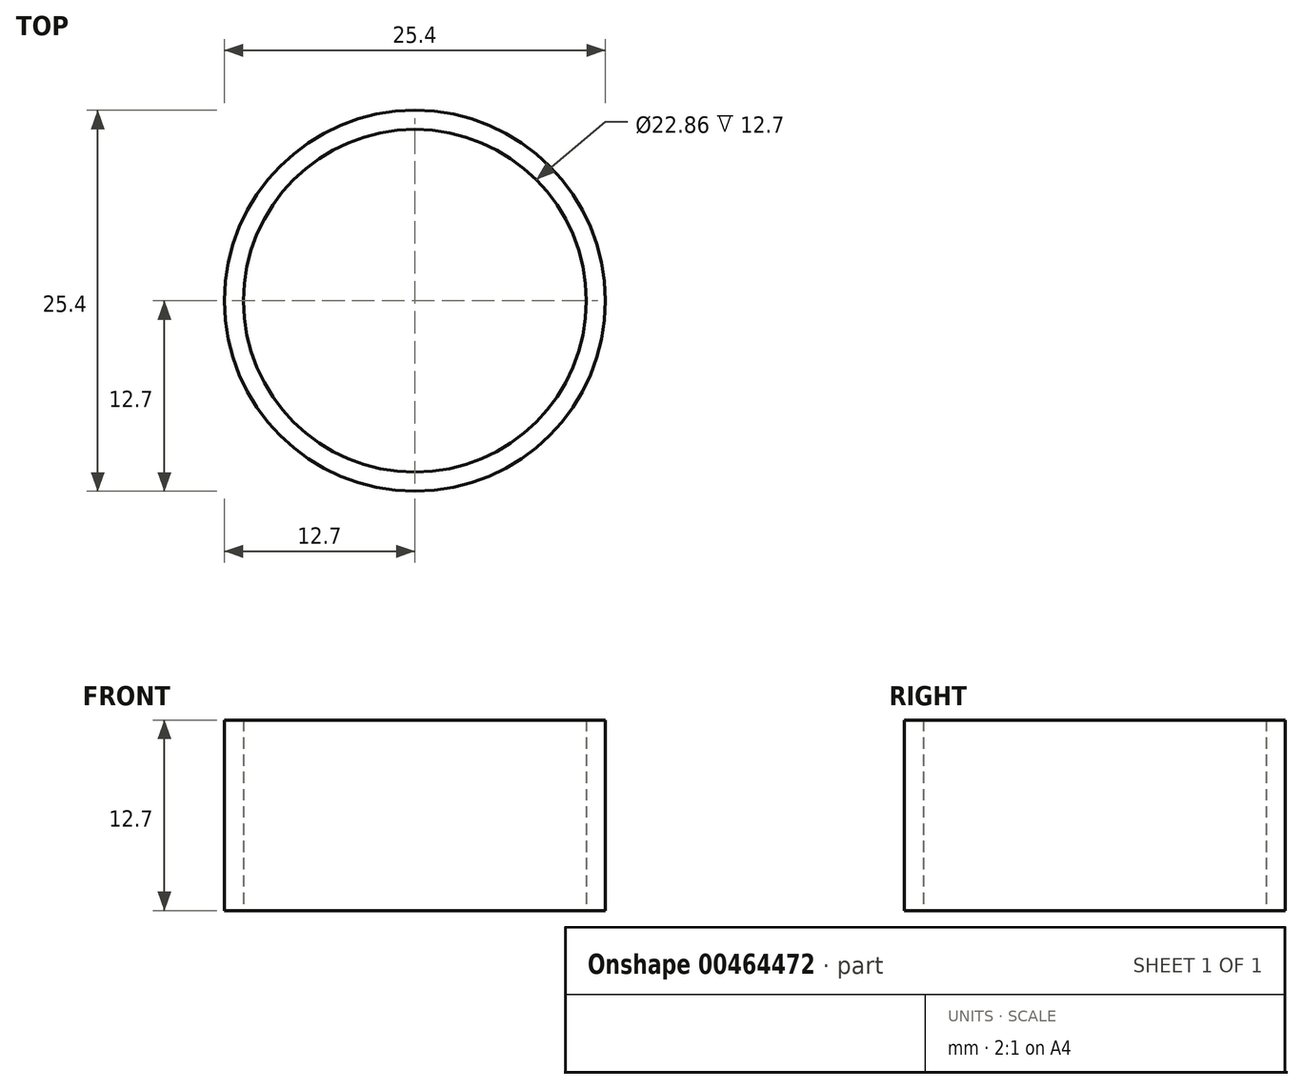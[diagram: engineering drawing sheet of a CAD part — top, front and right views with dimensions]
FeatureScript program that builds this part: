
annotation { "Feature Type Name" : "Feature", "Feature Type Description" : "" }
export const myFeature = defineFeature(function(context is Context, id is Id, definition is map)
    precondition{}
    {
        {
            var Q0;
            Q0=qCreatedBy(makeId("Top.planeOp"),FACE);
            var sketch = newSketch(context, id + "F0", { "sketchPlane" : qUnion([Q0])});
            skCircle(sketch, "E0", {"center": v(0, 0) * mm, "radius": 11.43 * mm});
            skCircle(sketch, "E1", {"center": v(0, 0) * mm, "radius": 12.7 * mm});
            skSolve(sketch);
        }
        {
            var Q0;
            Q0 = qSketchRegion(id + "F0", true);
            extrude(context, id + "F1", {"entities" : qUnion([Q0]), "depth" : 12.7 * mm});
        }
    });
